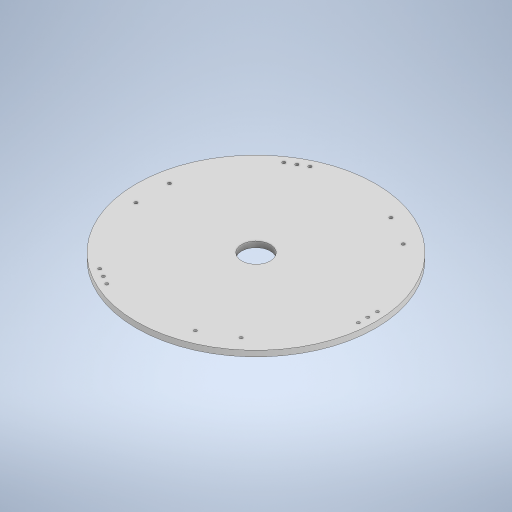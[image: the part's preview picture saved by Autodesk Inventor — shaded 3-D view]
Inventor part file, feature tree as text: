
AUTODESK INVENTOR PART (.ipt)
format: ipt  version: 2023 (Build 270158000, 158)  size: 259,072 bytes
history: native  units: mm
features: sketch x5, extrude x3, hole x2
ambient origin geometry x8: Origin, YZ Plane, XZ Plane, XY Plane, X Axis, Y Axis, Z Axis, Center Point
bodies: Body1 (feature_tree)
feature tree (10):
  sketch  "スケッチ1"
  sketch  "スケッチ2"
  extrude  "押し出し5"  Depth=250.0mm
  extrude  "押し出し6"  Depth=3.2mm
  hole  "穴1"  [1 undecoded]
  hole  "穴2"  [1 undecoded]
  extrude  "押し出し7"  Depth=30.0mm TaperAngle=360.0deg
  sketch  "スケッチ4"
  sketch  "スケッチ5"
  sketch  "スケッチ6"
note: 2 required parameter values undecoded (feature->parameter linkage not recoverable at this tier; creation-order binding heuristic only, values carry confidence <= 0.55)
